# Revit family: BC_Aircalo_BORA-60-STD-Droite_LOD200_
name_source: partatom
category: Equipement de génie climatique
revit_build: Autodesk Revit 2017 (Build: 20160225_1515(x64)
units: mm (PartAtom-declared; Revit-internal decimal feet)

## family parameters
Basée sur le plan de construction = Non
Cote de connecteur circulaire = Utiliser le diamètre
Couper avec des vides une fois chargée = Non
Numéro OmniClass = 23.75.70.17.27
Partagée = Non
Point de calcul de pièce = Non
Titre OmniClass = Fan Coil Units
Toujours verticalement = Non
Type d'élément = Normal

## types (2) — shared parameters
Connection Diameter = 12.70 mm
Fabricant = Aircalo
Filter class = G3;G4
Insulation Material = Mousse polyuréthane ignifugé 20mm
Length Cassette = 595.00 mm
Main Material = Acier galvanisé
Manufacturer Product Link = http://aircalo.fr
Modèle = Bora Standard
Motor power absorbed = 100 W
New Air Diameter = 125.00 mm
Nominal Voltage = 230 V
Outlet Diameter = 16.00 mm
Overall Length = 865.00 mm
Overall Width = 599.00 mm
Second Diameter = 12.70 mm
Thin line THK = 0.00 mm

## per-type parameters (varying)
| type | Mass | Overall Height | Product Code |
| Bora 60 Standard - Hauteur 300mm | 27.00 kg | 300.00 mm | B1A |
| Bora 60 Standard - Hauteur 380mm | 30.00 kg | 380.00 mm | B3A |

## geometry (parser evidence)
native form markers: Sweep x7
no freeform markers — native parametric forms only
